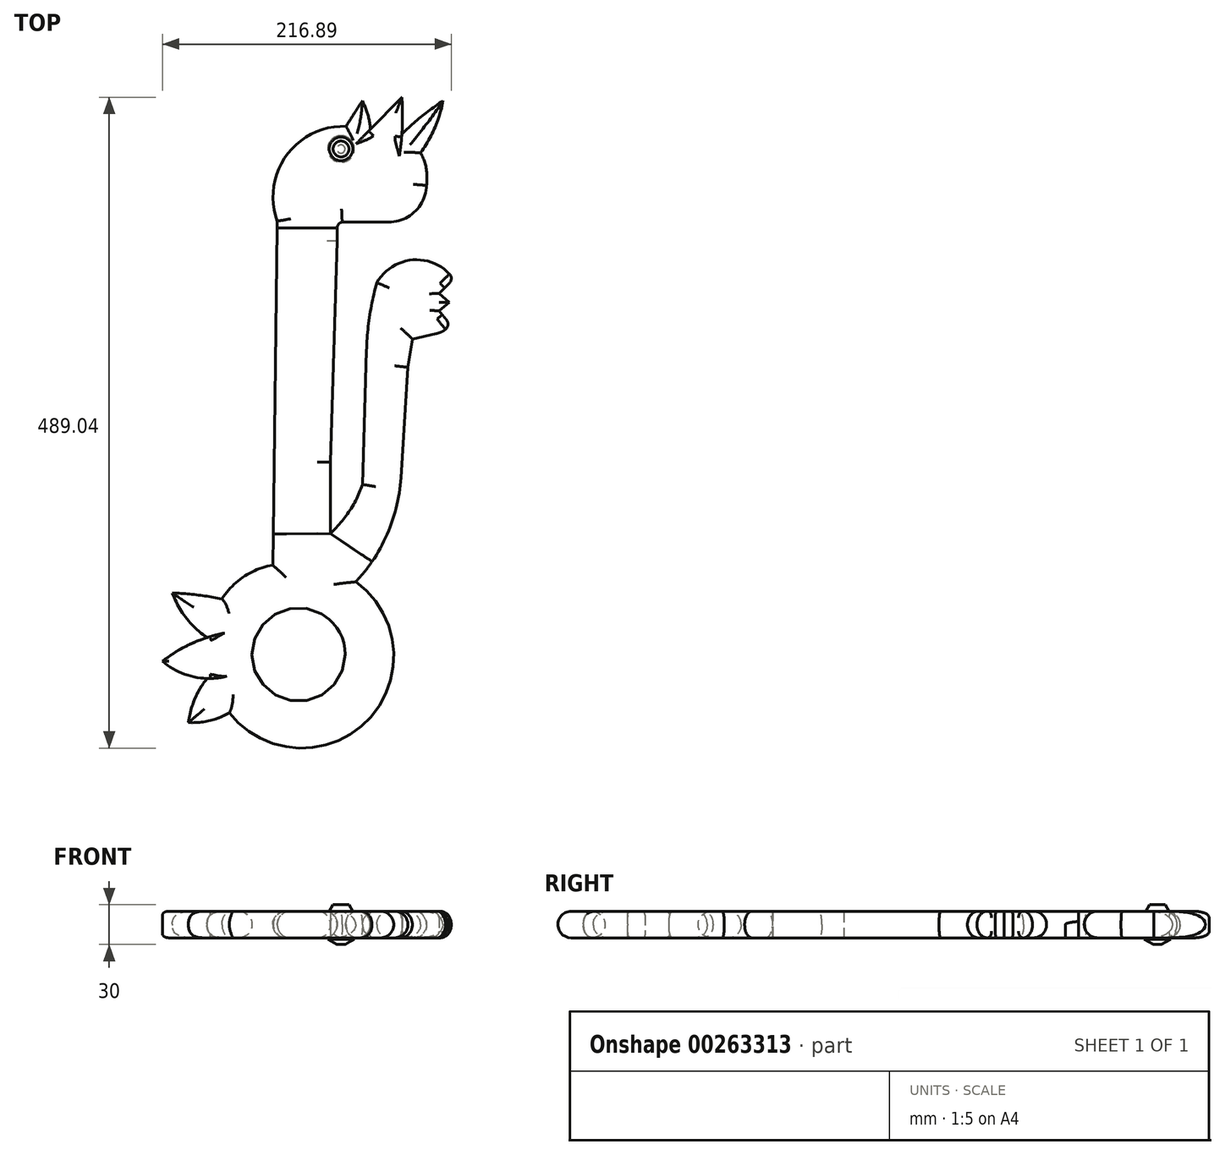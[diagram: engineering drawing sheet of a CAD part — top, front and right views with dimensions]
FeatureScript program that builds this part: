
annotation { "Feature Type Name" : "Feature", "Feature Type Description" : "" }
export const myFeature = defineFeature(function(context is Context, id is Id, definition is map)
    precondition{}
    {
        {
            var Q0;
            Q0=qCreatedBy(makeId("Top.planeOp"),FACE);
            var sketch = newSketch(context, id + "F0", { "sketchPlane" : qUnion([Q0])});
            skArc(sketch, "E0", {"start": v(-69.56, -48.3) * mm, "mid": v(-88.08, -45.25) * mm, "end": v(-106.8, -43.78) * mm});
            skArc(sketch, "E1", {"start": v(-106.8, -43.78) * mm, "mid": v(-96.39, -62.57) * mm, "end": v(-80.73, -77.27) * mm});
            skArc(sketch, "E2", {"start": v(-80.73, -77.27) * mm, "mid": v(-98.26, -84.7) * mm, "end": v(-114.23, -95.07) * mm});
            skArc(sketch, "E3", {"start": v(-114.23, -95.07) * mm, "mid": v(-98.6, -104.41) * mm, "end": v(-80.73, -107.98) * mm});
            skArc(sketch, "E4", {"start": v(-80.73, -107.98) * mm, "mid": v(-90.04, -123.58) * mm, "end": v(-94.69, -141.13) * mm});
            skArc(sketch, "E5", {"start": v(-94.69, -141.13) * mm, "mid": v(-78.8, -139.7) * mm, "end": v(-63.98, -133.8) * mm});
            skArc(sketch, "E6", {"start": v(-63.98, -133.8) * mm, "mid": v(40.14, -139.24) * mm, "end": v(30.94, -35.4) * mm});
            skArc(sketch, "E7", {"start": v(-31.41, -22.87) * mm, "mid": v(-53.17, -31.57) * mm, "end": v(-69.56, -48.3) * mm});
            skCircle(sketch, "E8", {"center": v(-12, -90) * mm, "radius": 35 * mm});
            skLineSegment(sketch, "E9", {"start": v(-12, -90) * mm, "end": v(-12, 0) * mm});
            skLineSegment(sketch, "E10", {"start": v(-12, 0) * mm, "end": v(0, 0) * mm});
            skLineSegment(sketch, "E11", {"start": v(-31.41, -22.87) * mm, "end": v(-12, 0) * mm});
            skLineSegment(sketch, "E12", {"start": v(-31.41, -22.87) * mm, "end": v(0, 0) * mm});
            skArc(sketch, "E13", {"start": v(30.94, -35.4) * mm, "mid": v(57.65, 8.29) * mm, "end": v(64.82, 58.99) * mm});
            skLineSegment(sketch, "E14", {"start": v(64.82, 42.9) * mm, "end": v(70.1, 125.75) * mm});
            skLineSegment(sketch, "E15", {"start": v(70.1, 125.75) * mm, "end": v(73.47, 146.99) * mm});
            skLineSegment(sketch, "E16", {"start": v(73.47, 146.99) * mm, "end": v(91.25, 150.97) * mm});
            skArc(sketch, "E17", {"start": v(93.55, 168.05) * mm, "mid": v(98.13, 170.3) * mm, "end": v(101.04, 174.5) * mm});
            skArc(sketch, "E18", {"start": v(101.04, 174.5) * mm, "mid": v(98.19, 178.86) * mm, "end": v(93.55, 181.22) * mm});
            skArc(sketch, "E19", {"start": v(91.25, 150.97) * mm, "mid": v(97.19, 153.5) * mm, "end": v(101.85, 157.96) * mm});
            skArc(sketch, "E20", {"start": v(101.85, 157.96) * mm, "mid": v(99.5, 164.5) * mm, "end": v(93.55, 168.05) * mm});
            skArc(sketch, "E21", {"start": v(93.55, 181.22) * mm, "mid": v(100.45, 185.24) * mm, "end": v(104.38, 192.2) * mm});
            skArc(sketch, "E22", {"start": v(16.27, 5.35) * mm, "mid": v(27.94, 20.47) * mm, "end": v(35.96, 37.8) * mm});
            skLineSegment(sketch, "E23", {"start": v(16.27, 5.35) * mm, "end": v(12.02, 0.97) * mm});
            skLineSegment(sketch, "E24", {"start": v(12.02, 54.47) * mm, "end": v(16.98, 220.58) * mm});
            skLineSegment(sketch, "E25", {"start": v(16.98, 220.58) * mm, "end": v(16.98, 230.48) * mm});
            skArc(sketch, "E26", {"start": v(20.74, 234.78) * mm, "mid": v(18.05, 233.34) * mm, "end": v(16.98, 230.48) * mm});
            skLineSegment(sketch, "E27", {"start": v(20.74, 234.78) * mm, "end": v(55.67, 234.78) * mm});
            skArc(sketch, "E28", {"start": v(55.67, 234.78) * mm, "mid": v(75.45, 242.82) * mm, "end": v(84, 262.38) * mm});
            skArc(sketch, "E29", {"start": v(84, 262.38) * mm, "mid": v(83.8, 275) * mm, "end": v(79.59, 286.9) * mm});
            skArc(sketch, "E30", {"start": v(79.59, 286.9) * mm, "mid": v(90.12, 305.47) * mm, "end": v(96.46, 325.87) * mm});
            skArc(sketch, "E31", {"start": v(96.46, 325.87) * mm, "mid": v(80.34, 314.22) * mm, "end": v(65.52, 300.95) * mm});
            skArc(sketch, "E32", {"start": v(65.52, 300.95) * mm, "mid": v(66.02, 314.82) * mm, "end": v(65.52, 328.68) * mm});
            skArc(sketch, "E33", {"start": v(41.86, 304.54) * mm, "mid": v(40.03, 315.53) * mm, "end": v(35.9, 325.87) * mm});
            skArc(sketch, "E34", {"start": v(35.9, 325.87) * mm, "mid": v(29.68, 316.4) * mm, "end": v(23.68, 306.81) * mm});
            skArc(sketch, "E35", {"start": v(23.68, 306.81) * mm, "mid": v(-21.12, 284.92) * mm, "end": v(-28, 235.53) * mm});
            skLineSegment(sketch, "E36", {"start": v(-31.41, -22.87) * mm, "end": v(-28, 235.53) * mm});
            skLineSegment(sketch, "E37", {"start": v(0, 0) * mm, "end": v(0, 302.13) * mm});
            skLineSegment(sketch, "E38", {"start": v(12.02, 0.97) * mm, "end": v(-31.41, -22.87) * mm});
            skLineSegment(sketch, "E39", {"start": v(0, 0) * mm, "end": v(12.02, 0.97) * mm});
            skLineSegment(sketch, "E40", {"start": v(12.02, 0.97) * mm, "end": v(30.94, -35.4) * mm});
            skLineSegment(sketch, "E41", {"start": v(64.82, 58.99) * mm, "end": v(46.6, 104.17) * mm});
            skLineSegment(sketch, "E42", {"start": v(12.02, 0.97) * mm, "end": v(12.02, 54.47) * mm});
            skLineSegment(sketch, "E43", {"start": v(-29.54, 119.27) * mm, "end": v(13.94, 118.7) * mm});
            skLineSegment(sketch, "E44", {"start": v(35.96, 37.8) * mm, "end": v(38.97, 138.47) * mm});
            skArc(sketch, "E45", {"start": v(104.38, 192.2) * mm, "mid": v(74.78, 206.52) * mm, "end": v(46.71, 189.39) * mm});
            skArc(sketch, "E46", {"start": v(46.71, 189.39) * mm, "mid": v(41.3, 164.16) * mm, "end": v(38.97, 138.47) * mm});
            skLineSegment(sketch, "E47", {"start": v(104.38, 192.2) * mm, "end": v(93.55, 181.22) * mm});
            skLineSegment(sketch, "E48", {"start": v(93.55, 168.05) * mm, "end": v(101.85, 157.96) * mm});
            skLineSegment(sketch, "E49", {"start": v(93.55, 181.22) * mm, "end": v(101.04, 174.5) * mm});
            skLineSegment(sketch, "E50", {"start": v(93.55, 168.05) * mm, "end": v(101.04, 174.5) * mm});
            skLineSegment(sketch, "E51", {"start": v(41.86, 304.54) * mm, "end": v(65.52, 328.68) * mm});
            skLineSegment(sketch, "E52", {"start": v(16.98, 230.48) * mm, "end": v(-28.07, 230.48) * mm});
            skLineSegment(sketch, "E53", {"start": v(12.02, 0.97) * mm, "end": v(-31.1, 0.49) * mm});
            skPoint(sketch, "E53.endSnap0", {"position": v(6.01, 0.49) * mm});
            skLineSegment(sketch, "E54", {"start": v(12.02, 0.97) * mm, "end": v(43.15, -20.17) * mm});
            skSolve(sketch);
        }
        {
            var Q0;
            {var subQ0=sQuery(id+"F0.wireOp",EDGE,"E38");var subQ1=sQuery(id+"F0.wireOp",EDGE,"E9");var subQ2=makeQuery(id+"F0.imprint","INTERSECT",VERTEX,{"derivedFrom":[subQ1,subQ0]});Q0=makeQuery(id+"F0.imprint","IMPRINT",FACE,{"disambiguationData":[TD([[makeQuery(id+"F0.imprint","IMPRINT",EDGE,{"disambiguationData":[TD([[subQ2,-1.0]])],"derivedFrom":subQ1}),1.0]])]});}
            var Q1;
            {var subQ0=sQuery(id+"F0.wireOp",EDGE,"E11");Q1=makeQuery(id+"F0.imprint","IMPRINT",FACE,{"disambiguationData":[TD([[makeQuery(id+"F0.imprint","IMPRINT",EDGE,{"derivedFrom":subQ0}),-1.0]])]});}
            var Q2;
            {var subQ0=sQuery(id+"F0.wireOp",EDGE,"E39");Q2=makeQuery(id+"F0.imprint","IMPRINT",FACE,{"disambiguationData":[TD([[makeQuery(id+"F0.imprint","IMPRINT",EDGE,{"derivedFrom":subQ0}),1.0]])]});}
            var Q3;
            Q3=makeQuery(id+"F0.imprint","IMPRINT",FACE,{"disambiguationData":[TD([[makeQuery(id+"F0.imprint","IMPRINT",EDGE,{"derivedFrom":sQuery(id+"F0.wireOp",EDGE,"E0")}),1.0]])]});
            var Q4;
            {var subQ5=sQuery(id+"F0.wireOp",EDGE,"E39");Q4=makeQuery(id+"F0.imprint","IMPRINT",FACE,{"disambiguationData":[TD([[makeQuery(id+"F0.imprint","IMPRINT",EDGE,{"derivedFrom":subQ5}),-1.0]])]});}
            var Q5;
            {var subQ2=sQuery(id+"F0.wireOp",EDGE,"E10");Q5=makeQuery(id+"F0.imprint","IMPRINT",FACE,{"disambiguationData":[TD([[makeQuery(id+"F0.imprint","IMPRINT",EDGE,{"derivedFrom":subQ2}),1.0]])]});}
            var Q6;
            {var subQ0=sQuery(id+"F0.wireOp",EDGE,"E10");Q6=makeQuery(id+"F0.imprint","IMPRINT",FACE,{"disambiguationData":[TD([[makeQuery(id+"F0.imprint","IMPRINT",EDGE,{"derivedFrom":subQ0}),-1.0]])]});}
            var Q7;
            {var subQ0=sQuery(id+"F0.wireOp",EDGE,"E40");Q7=makeQuery(id+"F0.imprint","IMPRINT",FACE,{"disambiguationData":[TD([[makeQuery(id+"F0.imprint","IMPRINT",EDGE,{"derivedFrom":subQ0}),1.0]])]});}
            extrude(context, id + "F1", {"entities" : qUnion([Q0, Q1, Q2, Q3, Q4, Q5, Q6, Q7]), "depth" : 20 * mm});
        }
        {
            var Q0;
            {var subQ1=sQuery(id+"F0.wireOp",EDGE,"E14");Q0=makeQuery(id+"F0.imprint","IMPRINT",FACE,{"disambiguationData":[TD([[makeQuery(id+"F0.imprint","IMPRINT",EDGE,{"derivedFrom":subQ1}),1.0]])]});}
            extrude(context, id + "F2", {"entities" : qUnion([Q0]), "depth" : 20 * mm});
        }
        {
            var Q0;
            {var subQ0=sQuery(id+"F0.wireOp",EDGE,"E43");var subQ1=sQuery(id+"F0.wireOp",EDGE,"E36");var subQ2=makeQuery(id+"F0.imprint","INTERSECT",VERTEX,{"derivedFrom":[subQ1,subQ0]});Q0=makeQuery(id+"F0.imprint","IMPRINT",FACE,{"disambiguationData":[TD([[makeQuery(id+"F0.imprint","IMPRINT",EDGE,{"disambiguationData":[TD([[subQ2,1.0]])],"derivedFrom":subQ1}),-1.0]])]});}
            var Q1;
            {var subQ5=sQuery(id+"F0.wireOp",EDGE,"E42");Q1=makeQuery(id+"F0.imprint","IMPRINT",FACE,{"disambiguationData":[TD([[makeQuery(id+"F0.imprint","IMPRINT",EDGE,{"derivedFrom":subQ5}),1.0]])]});}
            var Q2;
            {var subQ0=sQuery(id+"F0.wireOp",EDGE,"E43");var subQ1=sQuery(id+"F0.wireOp",EDGE,"E36");var subQ2=makeQuery(id+"F0.imprint","INTERSECT",VERTEX,{"derivedFrom":[subQ1,subQ0]});Q2=makeQuery(id+"F0.imprint","IMPRINT",FACE,{"disambiguationData":[TD([[makeQuery(id+"F0.imprint","IMPRINT",EDGE,{"disambiguationData":[TD([[subQ2,-1.0]])],"derivedFrom":subQ1}),-1.0]])]});}
            var Q3;
            {var subQ7=sQuery(id+"F0.wireOp",EDGE,"E25");Q3=makeQuery(id+"F0.imprint","IMPRINT",FACE,{"disambiguationData":[TD([[makeQuery(id+"F0.imprint","IMPRINT",EDGE,{"derivedFrom":subQ7}),1.0]])]});}
            extrude(context, id + "F3", {"entities" : qUnion([Q0, Q1, Q2, Q3]), "depth" : 20 * mm});
        }
        {
            var Q0;
            {var subQ0=sQuery(id+"F0.wireOp",EDGE,"E36");var subQ1=sQuery(id+"F0.wireOp",EDGE,"E35");var subQ2=makeQuery(id+"F0.imprint","INTERSECT",VERTEX,{"derivedFrom":[subQ1,subQ0]});Q0=makeQuery(id+"F0.imprint","IMPRINT",FACE,{"disambiguationData":[TD([[makeQuery(id+"F0.imprint","IMPRINT",EDGE,{"disambiguationData":[TD([[subQ2,1.0]])],"derivedFrom":subQ1}),1.0]])]});}
            var Q1;
            {var subQ4=sQuery(id+"F0.wireOp",EDGE,"E26");Q1=makeQuery(id+"F0.imprint","IMPRINT",FACE,{"disambiguationData":[TD([[makeQuery(id+"F0.imprint","IMPRINT",EDGE,{"derivedFrom":subQ4}),-1.0]])]});}
            extrude(context, id + "F4", {"entities" : qUnion([Q0, Q1]), "depth" : 20 * mm});
        }
        {
            var Q0;
            Q0=makeQuery(id+"F1.opExtrude","CAP_EDGE",EDGE,{"disambiguationData":[OSD([sQuery(id+"F0.wireOp",EDGE,"E36")])],"isStart":false});
            var Q1;
            Q1=makeQuery(id+"F1.opExtrude","CAP_EDGE",EDGE,{"disambiguationData":[OSD([sQuery(id+"F0.wireOp",EDGE,"E24")])],"isStart":false});
            var Q2;
            Q2=makeQuery(id+"F1.opExtrude","CAP_EDGE",EDGE,{"disambiguationData":[OSD([sQuery(id+"F0.wireOp",EDGE,"E42")])],"isStart":false});
            var Q3;
            Q3=makeQuery(id+"F1.opExtrude","CAP_EDGE",EDGE,{"disambiguationData":[OSD([sQuery(id+"F0.wireOp",EDGE,"E25")])],"isStart":false});
            var Q4;
            Q4=makeQuery(id+"F1.opExtrude","CAP_EDGE",EDGE,{"disambiguationData":[OSD([sQuery(id+"F0.wireOp",EDGE,"E35")])],"isStart":false});
            var Q5;
            Q5=makeQuery(id+"F1.opExtrude","CAP_EDGE",EDGE,{"disambiguationData":[OSD([sQuery(id+"F0.wireOp",EDGE,"E26")])],"isStart":false});
            var Q6;
            Q6=makeQuery(id+"F1.opExtrude","CAP_EDGE",EDGE,{"disambiguationData":[OSD([sQuery(id+"F0.wireOp",EDGE,"E42")])],"isStart":true});
            var Q7;
            Q7=makeQuery(id+"F1.opExtrude","CAP_EDGE",EDGE,{"disambiguationData":[OSD([sQuery(id+"F0.wireOp",EDGE,"E25")])],"isStart":true});
            var Q8;
            Q8=makeQuery(id+"F1.opExtrude","CAP_EDGE",EDGE,{"disambiguationData":[OSD([sQuery(id+"F0.wireOp",EDGE,"E36")])],"isStart":true});
            var Q9;
            Q9=makeQuery(id+"F1.opExtrude","CAP_EDGE",EDGE,{"disambiguationData":[OSD([sQuery(id+"F0.wireOp",EDGE,"E35")])],"isStart":true});
            var Q10;
            Q10=makeQuery(id+"F1.opExtrude","CAP_EDGE",EDGE,{"disambiguationData":[OSD([sQuery(id+"F0.wireOp",EDGE,"E26")])],"isStart":true});
            var Q11;
            Q11=makeQuery(id+"F1.opExtrude","CAP_EDGE",EDGE,{"disambiguationData":[OSD([sQuery(id+"F0.wireOp",EDGE,"E22")])],"isStart":false});
            var Q12;
            Q12=makeQuery(id+"F1.opExtrude","CAP_EDGE",EDGE,{"disambiguationData":[OSD([sQuery(id+"F0.wireOp",EDGE,"E23")])],"isStart":false});
            var Q13;
            Q13=makeQuery(id+"F1.opExtrude","CAP_EDGE",EDGE,{"disambiguationData":[OSD([sQuery(id+"F0.wireOp",EDGE,"E44")])],"isStart":false});
            var Q14;
            Q14=makeQuery(id+"F1.opExtrude","CAP_EDGE",EDGE,{"disambiguationData":[OSD([sQuery(id+"F0.wireOp",EDGE,"E45")])],"isStart":false});
            var Q15;
            Q15=makeQuery(id+"F1.opExtrude","CAP_EDGE",EDGE,{"disambiguationData":[OSD([sQuery(id+"F0.wireOp",EDGE,"E22")])],"isStart":true});
            var Q16;
            Q16=makeQuery(id+"F1.opExtrude","CAP_EDGE",EDGE,{"disambiguationData":[OSD([sQuery(id+"F0.wireOp",EDGE,"E44")])],"isStart":true});
            var Q17;
            Q17=makeQuery(id+"F1.opExtrude","CAP_EDGE",EDGE,{"disambiguationData":[OSD([sQuery(id+"F0.wireOp",EDGE,"E45")])],"isStart":true});
            var Q18;
            Q18=makeQuery(id+"F1.opExtrude","CAP_EDGE",EDGE,{"disambiguationData":[OSD([sQuery(id+"F0.wireOp",EDGE,"E13")])],"isStart":false});
            var Q19;
            Q19=makeQuery(id+"F1.opExtrude","CAP_EDGE",EDGE,{"disambiguationData":[OSD([sQuery(id+"F0.wireOp",EDGE,"E14")])],"isStart":false});
            var Q20;
            Q20=makeQuery(id+"F1.opExtrude","CAP_EDGE",EDGE,{"disambiguationData":[OSD([sQuery(id+"F0.wireOp",EDGE,"E15")])],"isStart":false});
            var Q21;
            Q21=makeQuery(id+"F1.opExtrude","CAP_EDGE",EDGE,{"disambiguationData":[OSD([sQuery(id+"F0.wireOp",EDGE,"E16")])],"isStart":false});
            var Q22;
            Q22=makeQuery(id+"F1.opExtrude","CAP_EDGE",EDGE,{"disambiguationData":[OSD([sQuery(id+"F0.wireOp",EDGE,"E16")])],"isStart":true});
            var Q23;
            Q23=makeQuery(id+"F1.opExtrude","CAP_EDGE",EDGE,{"disambiguationData":[OSD([sQuery(id+"F0.wireOp",EDGE,"E15")])],"isStart":true});
            var Q24;
            Q24=makeQuery(id+"F1.opExtrude","CAP_EDGE",EDGE,{"disambiguationData":[OSD([sQuery(id+"F0.wireOp",EDGE,"E14")])],"isStart":true});
            var Q25;
            Q25=makeQuery(id+"F1.opExtrude","CAP_EDGE",EDGE,{"disambiguationData":[OSD([sQuery(id+"F0.wireOp",EDGE,"E13")])],"isStart":true});
            var Q26;
            Q26=makeQuery(id+"F1.opExtrude","CAP_EDGE",EDGE,{"disambiguationData":[OSD([sQuery(id+"F0.wireOp",EDGE,"E6")])],"isStart":false});
            var Q27;
            Q27=makeQuery(id+"F1.opExtrude","CAP_EDGE",EDGE,{"disambiguationData":[OSD([sQuery(id+"F0.wireOp",EDGE,"E8")])],"isStart":false});
            var Q28;
            Q28=makeQuery(id+"F1.opExtrude","CAP_EDGE",EDGE,{"disambiguationData":[OSD([sQuery(id+"F0.wireOp",EDGE,"E7")])],"isStart":false});
            var Q29;
            Q29=makeQuery(id+"F1.opExtrude","CAP_EDGE",EDGE,{"disambiguationData":[OSD([sQuery(id+"F0.wireOp",EDGE,"E8")])],"isStart":true});
            var Q30;
            Q30=makeQuery(id+"F1.opExtrude","CAP_EDGE",EDGE,{"disambiguationData":[OSD([sQuery(id+"F0.wireOp",EDGE,"E7")])],"isStart":true});
            var Q31;
            Q31=makeQuery(id+"F1.opExtrude","CAP_EDGE",EDGE,{"disambiguationData":[OSD([sQuery(id+"F0.wireOp",EDGE,"E6")])],"isStart":true});
            fillet(context, id + "F5", {"entities" : qUnion([Q0, Q1, Q2, Q3, Q4, Q5, Q6, Q7, Q8, Q9, Q10, Q11, Q12, Q13, Q14, Q15, Q16, Q17, Q18, Q19, Q20, Q21, Q22, Q23, Q24, Q25, Q26, Q27, Q28, Q29, Q30, Q31]), "radius" : 10 * mm, "tangentPropagation" : true, "allowEdgeOverflow" : false});
        }
        {
            var Q0;
            Q0=makeQuery(id+"F1.opExtrude","CAP_EDGE",EDGE,{"disambiguationData":[OSD([sQuery(id+"F0.wireOp",EDGE,"E0")])],"isStart":false});
            var Q1;
            Q1=makeQuery(id+"F1.opExtrude","CAP_EDGE",EDGE,{"disambiguationData":[OSD([sQuery(id+"F0.wireOp",EDGE,"E1")])],"isStart":false});
            var Q2;
            Q2=makeQuery(id+"F1.opExtrude","CAP_EDGE",EDGE,{"disambiguationData":[OSD([sQuery(id+"F0.wireOp",EDGE,"E5")])],"isStart":false});
            var Q3;
            Q3=makeQuery(id+"F1.opExtrude","CAP_EDGE",EDGE,{"disambiguationData":[OSD([sQuery(id+"F0.wireOp",EDGE,"E4")])],"isStart":false});
            var Q4;
            Q4=makeQuery(id+"F1.opExtrude","CAP_EDGE",EDGE,{"disambiguationData":[OSD([sQuery(id+"F0.wireOp",EDGE,"E0")])],"isStart":true});
            var Q5;
            Q5=makeQuery(id+"F1.opExtrude","CAP_EDGE",EDGE,{"disambiguationData":[OSD([sQuery(id+"F0.wireOp",EDGE,"E1")])],"isStart":true});
            var Q6;
            Q6=makeQuery(id+"F1.opExtrude","CAP_EDGE",EDGE,{"disambiguationData":[OSD([sQuery(id+"F0.wireOp",EDGE,"E4")])],"isStart":true});
            var Q7;
            Q7=makeQuery(id+"F1.opExtrude","CAP_EDGE",EDGE,{"disambiguationData":[OSD([sQuery(id+"F0.wireOp",EDGE,"E5")])],"isStart":true});
            fillet(context, id + "F6", {"entities" : qUnion([Q0, Q1, Q2, Q3, Q4, Q5, Q6, Q7]), "radius" : 9.5 * mm, "tangentPropagation" : true, "rho" : 0.5, "crossSection" : FilletCrossSection.CONIC, "allowEdgeOverflow" : false});
        }
        {
            var Q0;
            Q0=makeQuery(id+"F1.opExtrude","CAP_EDGE",EDGE,{"disambiguationData":[OSD([sQuery(id+"F0.wireOp",EDGE,"E3")])],"isStart":true});
            var Q1;
            Q1=makeQuery(id+"F1.opExtrude","CAP_EDGE",EDGE,{"disambiguationData":[OSD([sQuery(id+"F0.wireOp",EDGE,"E2")])],"isStart":true});
            var Q2;
            Q2=makeQuery(id+"F1.opExtrude","CAP_EDGE",EDGE,{"disambiguationData":[OSD([sQuery(id+"F0.wireOp",EDGE,"E2")])],"isStart":false});
            var Q3;
            Q3=makeQuery(id+"F1.opExtrude","CAP_EDGE",EDGE,{"disambiguationData":[OSD([sQuery(id+"F0.wireOp",EDGE,"E3")])],"isStart":false});
            fillet(context, id + "F7", {"entities" : qUnion([Q0, Q1, Q2, Q3]), "radius" : 3 * mm, "tangentPropagation" : true, "allowEdgeOverflow" : false});
        }
        {
            var Q0;
            Q0=makeQuery(id+"F2.opExtrude","CAP_EDGE",EDGE,{"disambiguationData":[OSD([sQuery(id+"F0.wireOp",EDGE,"E14")])],"isStart":false});
            var Q1;
            Q1=makeQuery(id+"F2.opExtrude","CAP_EDGE",EDGE,{"disambiguationData":[OSD([sQuery(id+"F0.wireOp",EDGE,"E15")])],"isStart":false});
            var Q2;
            Q2=makeQuery(id+"F2.opExtrude","CAP_EDGE",EDGE,{"disambiguationData":[OSD([sQuery(id+"F0.wireOp",EDGE,"E14")])],"isStart":true});
            var Q3;
            Q3=makeQuery(id+"F2.opExtrude","CAP_EDGE",EDGE,{"disambiguationData":[OSD([sQuery(id+"F0.wireOp",EDGE,"E15")])],"isStart":true});
            var Q4;
            Q4=makeQuery(id+"F2.opExtrude","CAP_EDGE",EDGE,{"disambiguationData":[OSD([sQuery(id+"F0.wireOp",EDGE,"E16")])],"isStart":true});
            var Q5;
            Q5=makeQuery(id+"F2.opExtrude","CAP_EDGE",EDGE,{"disambiguationData":[OSD([sQuery(id+"F0.wireOp",EDGE,"E16")])],"isStart":false});
            var Q6;
            Q6=makeQuery(id+"F2.opExtrude","CAP_EDGE",EDGE,{"disambiguationData":[OSD([sQuery(id+"F0.wireOp",EDGE,"E45")])],"isStart":true});
            var Q7;
            Q7=makeQuery(id+"F2.opExtrude","CAP_EDGE",EDGE,{"disambiguationData":[OSD([sQuery(id+"F0.wireOp",EDGE,"E45")])],"isStart":false});
            var Q8;
            Q8=makeQuery(id+"F2.opExtrude","CAP_EDGE",EDGE,{"disambiguationData":[OSD([sQuery(id+"F0.wireOp",EDGE,"E46")])],"isStart":false});
            var Q9;
            Q9=makeQuery(id+"F2.opExtrude","CAP_EDGE",EDGE,{"disambiguationData":[OSD([sQuery(id+"F0.wireOp",EDGE,"E44")])],"isStart":false});
            var Q10;
            Q10=makeQuery(id+"F2.opExtrude","CAP_EDGE",EDGE,{"disambiguationData":[OSD([sQuery(id+"F0.wireOp",EDGE,"E22")])],"isStart":false});
            var Q11;
            Q11=makeQuery(id+"F2.opExtrude","CAP_EDGE",EDGE,{"disambiguationData":[OSD([sQuery(id+"F0.wireOp",EDGE,"E23")])],"isStart":false});
            var Q12;
            Q12=makeQuery(id+"F2.opExtrude","CAP_EDGE",EDGE,{"disambiguationData":[OSD([sQuery(id+"F0.wireOp",EDGE,"E46")])],"isStart":true});
            var Q13;
            Q13=makeQuery(id+"F2.opExtrude","CAP_EDGE",EDGE,{"disambiguationData":[OSD([sQuery(id+"F0.wireOp",EDGE,"E23")])],"isStart":true});
            var Q14;
            Q14=makeQuery(id+"F2.opExtrude","CAP_EDGE",EDGE,{"disambiguationData":[OSD([sQuery(id+"F0.wireOp",EDGE,"E22")])],"isStart":true});
            var Q15;
            Q15=makeQuery(id+"F2.opExtrude","CAP_EDGE",EDGE,{"disambiguationData":[OSD([sQuery(id+"F0.wireOp",EDGE,"E44")])],"isStart":true});
            var Q16;
            Q16=makeQuery(id+"F3.opExtrude","CAP_EDGE",EDGE,{"disambiguationData":[OSD([sQuery(id+"F0.wireOp",EDGE,"E24")])],"isStart":false});
            var Q17;
            Q17=makeQuery(id+"F3.opExtrude","CAP_EDGE",EDGE,{"disambiguationData":[OSD([sQuery(id+"F0.wireOp",EDGE,"E42")])],"isStart":false});
            var Q18;
            Q18=makeQuery(id+"F3.opExtrude","CAP_EDGE",EDGE,{"disambiguationData":[OSD([sQuery(id+"F0.wireOp",EDGE,"E42")])],"isStart":true});
            var Q19;
            Q19=makeQuery(id+"F3.opExtrude","CAP_EDGE",EDGE,{"disambiguationData":[OSD([sQuery(id+"F0.wireOp",EDGE,"E24")])],"isStart":true});
            var Q20;
            Q20=makeQuery(id+"F3.opExtrude","CAP_EDGE",EDGE,{"disambiguationData":[OSD([sQuery(id+"F0.wireOp",EDGE,"E25")])],"isStart":true});
            var Q21;
            Q21=makeQuery(id+"F3.opExtrude","CAP_EDGE",EDGE,{"disambiguationData":[OSD([sQuery(id+"F0.wireOp",EDGE,"E36")])],"isStart":false});
            var Q22;
            Q22=makeQuery(id+"F3.opExtrude","CAP_EDGE",EDGE,{"disambiguationData":[OSD([sQuery(id+"F0.wireOp",EDGE,"E36")])],"isStart":true});
            var Q23;
            Q23=makeQuery(id+"F4.opExtrude","CAP_EDGE",EDGE,{"disambiguationData":[OSD([sQuery(id+"F0.wireOp",EDGE,"E36")])],"isStart":true});
            var Q24;
            Q24=makeQuery(id+"F4.opExtrude","CAP_EDGE",EDGE,{"disambiguationData":[OSD([sQuery(id+"F0.wireOp",EDGE,"E36")])],"isStart":false});
            var Q25;
            Q25=makeQuery(id+"F4.opExtrude","CAP_EDGE",EDGE,{"disambiguationData":[OSD([sQuery(id+"F0.wireOp",EDGE,"E35")])],"isStart":true});
            var Q26;
            Q26=makeQuery(id+"F4.opExtrude","CAP_EDGE",EDGE,{"disambiguationData":[OSD([sQuery(id+"F0.wireOp",EDGE,"E35")])],"isStart":false});
            var Q27;
            Q27=makeQuery(id+"F4.opExtrude","CAP_EDGE",EDGE,{"disambiguationData":[OSD([sQuery(id+"F0.wireOp",EDGE,"E27")])],"isStart":false});
            var Q28;
            Q28=makeQuery(id+"F4.opExtrude","CAP_EDGE",EDGE,{"disambiguationData":[OSD([sQuery(id+"F0.wireOp",EDGE,"E28")])],"isStart":false});
            var Q29;
            Q29=makeQuery(id+"F4.opExtrude","CAP_EDGE",EDGE,{"disambiguationData":[OSD([sQuery(id+"F0.wireOp",EDGE,"E29")])],"isStart":false});
            var Q30;
            Q30=makeQuery(id+"F4.opExtrude","CAP_EDGE",EDGE,{"disambiguationData":[OSD([sQuery(id+"F0.wireOp",EDGE,"E27")])],"isStart":true});
            var Q31;
            Q31=makeQuery(id+"F4.opExtrude","CAP_EDGE",EDGE,{"disambiguationData":[OSD([sQuery(id+"F0.wireOp",EDGE,"E28")])],"isStart":true});
            var Q32;
            Q32=makeQuery(id+"F4.opExtrude","CAP_EDGE",EDGE,{"disambiguationData":[OSD([sQuery(id+"F0.wireOp",EDGE,"E29")])],"isStart":true});
            var Q33;
            Q33=makeQuery(id+"F4.opExtrude","CAP_EDGE",EDGE,{"disambiguationData":[OSD([sQuery(id+"F0.wireOp",EDGE,"E26")])],"isStart":false});
            var Q34;
            Q34=makeQuery(id+"F4.opExtrude","CAP_EDGE",EDGE,{"disambiguationData":[OSD([sQuery(id+"F0.wireOp",EDGE,"E26")])],"isStart":true});
            var Q35;
            Q35=makeQuery(id+"F4.opExtrude","CAP_EDGE",EDGE,{"disambiguationData":[OSD([sQuery(id+"F0.wireOp",EDGE,"E30")])],"isStart":false});
            var Q36;
            Q36=makeQuery(id+"F4.opExtrude","CAP_EDGE",EDGE,{"disambiguationData":[OSD([sQuery(id+"F0.wireOp",EDGE,"E31")])],"isStart":false});
            var Q37;
            Q37=makeQuery(id+"F4.opExtrude","CAP_EDGE",EDGE,{"disambiguationData":[OSD([sQuery(id+"F0.wireOp",EDGE,"E30")])],"isStart":true});
            var Q38;
            Q38=makeQuery(id+"F4.opExtrude","CAP_EDGE",EDGE,{"disambiguationData":[OSD([sQuery(id+"F0.wireOp",EDGE,"E31")])],"isStart":true});
            var Q39;
            Q39=makeQuery(id+"F4.opExtrude","CAP_EDGE",EDGE,{"disambiguationData":[OSD([sQuery(id+"F0.wireOp",EDGE,"E33")])],"isStart":false});
            var Q40;
            Q40=makeQuery(id+"F4.opExtrude","CAP_EDGE",EDGE,{"disambiguationData":[OSD([sQuery(id+"F0.wireOp",EDGE,"E34")])],"isStart":false});
            var Q41;
            Q41=makeQuery(id+"F4.opExtrude","CAP_EDGE",EDGE,{"disambiguationData":[OSD([sQuery(id+"F0.wireOp",EDGE,"E34")])],"isStart":true});
            var Q42;
            Q42=makeQuery(id+"F4.opExtrude","CAP_EDGE",EDGE,{"disambiguationData":[OSD([sQuery(id+"F0.wireOp",EDGE,"E33")])],"isStart":true});
            fillet(context, id + "F8", {"entities" : qUnion([Q0, Q1, Q2, Q3, Q4, Q5, Q6, Q7, Q8, Q9, Q10, Q11, Q12, Q13, Q14, Q15, Q16, Q17, Q18, Q19, Q20, Q21, Q22, Q23, Q24, Q25, Q26, Q27, Q28, Q29, Q30, Q31, Q32, Q33, Q34, Q35, Q36, Q37, Q38, Q39, Q40, Q41, Q42]), "radius" : 10 * mm, "tangentPropagation" : true, "allowEdgeOverflow" : false});
        }
        {
            var Q0;
            Q0=makeQuery(id+"F4.opExtrude","CAP_EDGE",EDGE,{"disambiguationData":[OSD([sQuery(id+"F0.wireOp",EDGE,"E51")])],"isStart":false});
            var Q1;
            Q1=makeQuery(id+"F4.opExtrude","CAP_EDGE",EDGE,{"disambiguationData":[OSD([sQuery(id+"F0.wireOp",EDGE,"E32")])],"isStart":false});
            var Q2;
            Q2=makeQuery(id+"F4.opExtrude","CAP_EDGE",EDGE,{"disambiguationData":[OSD([sQuery(id+"F0.wireOp",EDGE,"E32")])],"isStart":true});
            var Q3;
            Q3=makeQuery(id+"F4.opExtrude","CAP_EDGE",EDGE,{"disambiguationData":[OSD([sQuery(id+"F0.wireOp",EDGE,"E51")])],"isStart":true});
            fillet(context, id + "F9", {"entities" : qUnion([Q0, Q1, Q2, Q3]), "radius" : 5 * mm, "tangentPropagation" : true, "allowEdgeOverflow" : false});
        }
        {
            var Q0;
            Q0=makeQuery(id+"F2.opExtrude","CAP_EDGE",EDGE,{"disambiguationData":[OSD([sQuery(id+"F0.wireOp",EDGE,"E50")])],"isStart":true});
            var Q1;
            Q1=makeQuery(id+"F2.opExtrude","CAP_EDGE",EDGE,{"disambiguationData":[OSD([sQuery(id+"F0.wireOp",EDGE,"E49")])],"isStart":true});
            var Q2;
            Q2=makeQuery(id+"F2.opExtrude","CAP_EDGE",EDGE,{"disambiguationData":[OSD([sQuery(id+"F0.wireOp",EDGE,"E49")])],"isStart":false});
            var Q3;
            Q3=makeQuery(id+"F2.opExtrude","CAP_EDGE",EDGE,{"disambiguationData":[OSD([sQuery(id+"F0.wireOp",EDGE,"E50")])],"isStart":false});
            var Q4;
            Q4=makeQuery(id+"F8.opFillet","BLEND_EDGE",EDGE,{"blendedFrom":[makeQuery(id+"F2.opExtrude","CAP_EDGE",EDGE,{"disambiguationData":[OSD([sQuery(id+"F0.wireOp",EDGE,"E45")])],"isStart":false}),makeQuery(id+"F2.opExtrude","SWEPT_FACE",FACE,{"disambiguationData":[OSD([sQuery(id+"F0.wireOp",EDGE,"E47")])]})],"blendedInto":[makeQuery(id+"F2.opExtrude","SWEPT_FACE",FACE,{"disambiguationData":[OSD([sQuery(id+"F0.wireOp",EDGE,"E47")])]})]});
            var Q5;
            Q5=makeQuery(id+"F8.opFillet","BLEND_EDGE",EDGE,{"blendedFrom":[makeQuery(id+"F2.opExtrude","CAP_EDGE",EDGE,{"disambiguationData":[OSD([sQuery(id+"F0.wireOp",EDGE,"E19")])],"isStart":false}),makeQuery(id+"F2.opExtrude","SWEPT_FACE",FACE,{"disambiguationData":[OSD([sQuery(id+"F0.wireOp",EDGE,"E48")])]})],"blendedInto":[makeQuery(id+"F2.opExtrude","SWEPT_FACE",FACE,{"disambiguationData":[OSD([sQuery(id+"F0.wireOp",EDGE,"E48")])]})]});
            fillet(context, id + "F10", {"entities" : qUnion([Q0, Q1, Q2, Q3, Q4, Q5]), "radius" : 5 * mm, "tangentPropagation" : true, "allowEdgeOverflow" : false});
        }
        {
            var Q0;
            Q0=makeQuery(id+"F5.opFillet","SPLIT",FACE,{"disambiguationData":[OD(0.0)],"derivedFrom":makeQuery(id+"F1.opExtrude","CAP_FACE",FACE,{"disambiguationData":[OSD([sQuery(id+"F0.wireOp",EDGE,"E0"),sQuery(id+"F0.wireOp",EDGE,"E1"),sQuery(id+"F0.wireOp",EDGE,"E2"),sQuery(id+"F0.wireOp",EDGE,"E3"),sQuery(id+"F0.wireOp",EDGE,"E4"),sQuery(id+"F0.wireOp",EDGE,"E5"),sQuery(id+"F0.wireOp",EDGE,"E6"),sQuery(id+"F0.wireOp",EDGE,"E7"),sQuery(id+"F0.wireOp",EDGE,"E8"),sQuery(id+"F0.wireOp",EDGE,"E13"),sQuery(id+"F0.wireOp",EDGE,"E14"),sQuery(id+"F0.wireOp",EDGE,"E15"),sQuery(id+"F0.wireOp",EDGE,"E16"),sQuery(id+"F0.wireOp",EDGE,"E19"),sQuery(id+"F0.wireOp",EDGE,"E22"),sQuery(id+"F0.wireOp",EDGE,"E23"),sQuery(id+"F0.wireOp",EDGE,"E24"),sQuery(id+"F0.wireOp",EDGE,"E25"),sQuery(id+"F0.wireOp",EDGE,"E26"),sQuery(id+"F0.wireOp",EDGE,"E27"),sQuery(id+"F0.wireOp",EDGE,"E28"),sQuery(id+"F0.wireOp",EDGE,"E29"),sQuery(id+"F0.wireOp",EDGE,"E30"),sQuery(id+"F0.wireOp",EDGE,"E31"),sQuery(id+"F0.wireOp",EDGE,"E32"),sQuery(id+"F0.wireOp",EDGE,"E33"),sQuery(id+"F0.wireOp",EDGE,"E34"),sQuery(id+"F0.wireOp",EDGE,"E35"),sQuery(id+"F0.wireOp",EDGE,"E36"),sQuery(id+"F0.wireOp",EDGE,"E42"),sQuery(id+"F0.wireOp",EDGE,"E44"),sQuery(id+"F0.wireOp",EDGE,"E45"),sQuery(id+"F0.wireOp",EDGE,"E46"),sQuery(id+"F0.wireOp",EDGE,"E47"),sQuery(id+"F0.wireOp",EDGE,"E48"),sQuery(id+"F0.wireOp",EDGE,"E49"),sQuery(id+"F0.wireOp",EDGE,"E50"),sQuery(id+"F0.wireOp",EDGE,"E51")])],"isStart":false})});
            var sketch = newSketch(context, id + "F11", { "sketchPlane" : qUnion([Q0])});
            skLineSegment(sketch, "E55", {"start": v(0, 0) * mm, "end": v(3.83, 289.97) * mm});
            skLineSegment(sketch, "E56", {"start": v(3.83, 289.97) * mm, "end": v(19.83, 289.76) * mm});
            skCircle(sketch, "E57", {"center": v(19.83, 289.76) * mm, "radius": 10 * mm});
            skSolve(sketch);
        }
        {
            var Q0;
            Q0=makeQuery(id+"F11.imprint","IMPRINT",FACE,{"disambiguationData":[TD([[makeQuery(id+"F11.imprint","IMPRINT",EDGE,{"derivedFrom":sQuery(id+"F11.wireOp",EDGE,"E57")}),1.0]])]});
            extrude(context, id + "F12", {"entities" : qUnion([Q0]), "operationType" : NewBodyOperationType.ADD, "depth" : 5 * mm, "hasSecondDirection" : true, "secondDirectionOppositeDirection" : true, "secondDirectionDepth" : 25 * mm});
        }
        {
            var Q0;
            Q0=makeQuery(id+"F12.opExtrude","CAP_EDGE",EDGE,{"disambiguationData":[OSD([sQuery(id+"F11.wireOp",EDGE,"E57")])],"isStart":false});
            chamfer(context, id + "F13", {"entities" : qUnion([Q0]), "chamferType" : ChamferType.OFFSET_ANGLE, "width" : 7 * mm, "oppositeDirection" : false, "angle" : 30 * degree, "tangentPropagation" : true});
        }
        {
            var Q0;
            Q0=makeQuery(id+"F12.opExtrude","CAP_EDGE",EDGE,{"disambiguationData":[OSD([sQuery(id+"F11.wireOp",EDGE,"E57")])],"isStart":true});
            chamfer(context, id + "F14", {"entities" : qUnion([Q0]), "chamferType" : ChamferType.OFFSET_ANGLE, "width" : 4 * mm, "oppositeDirection" : false, "angle" : 60 * degree, "tangentPropagation" : true});
        }
    });
